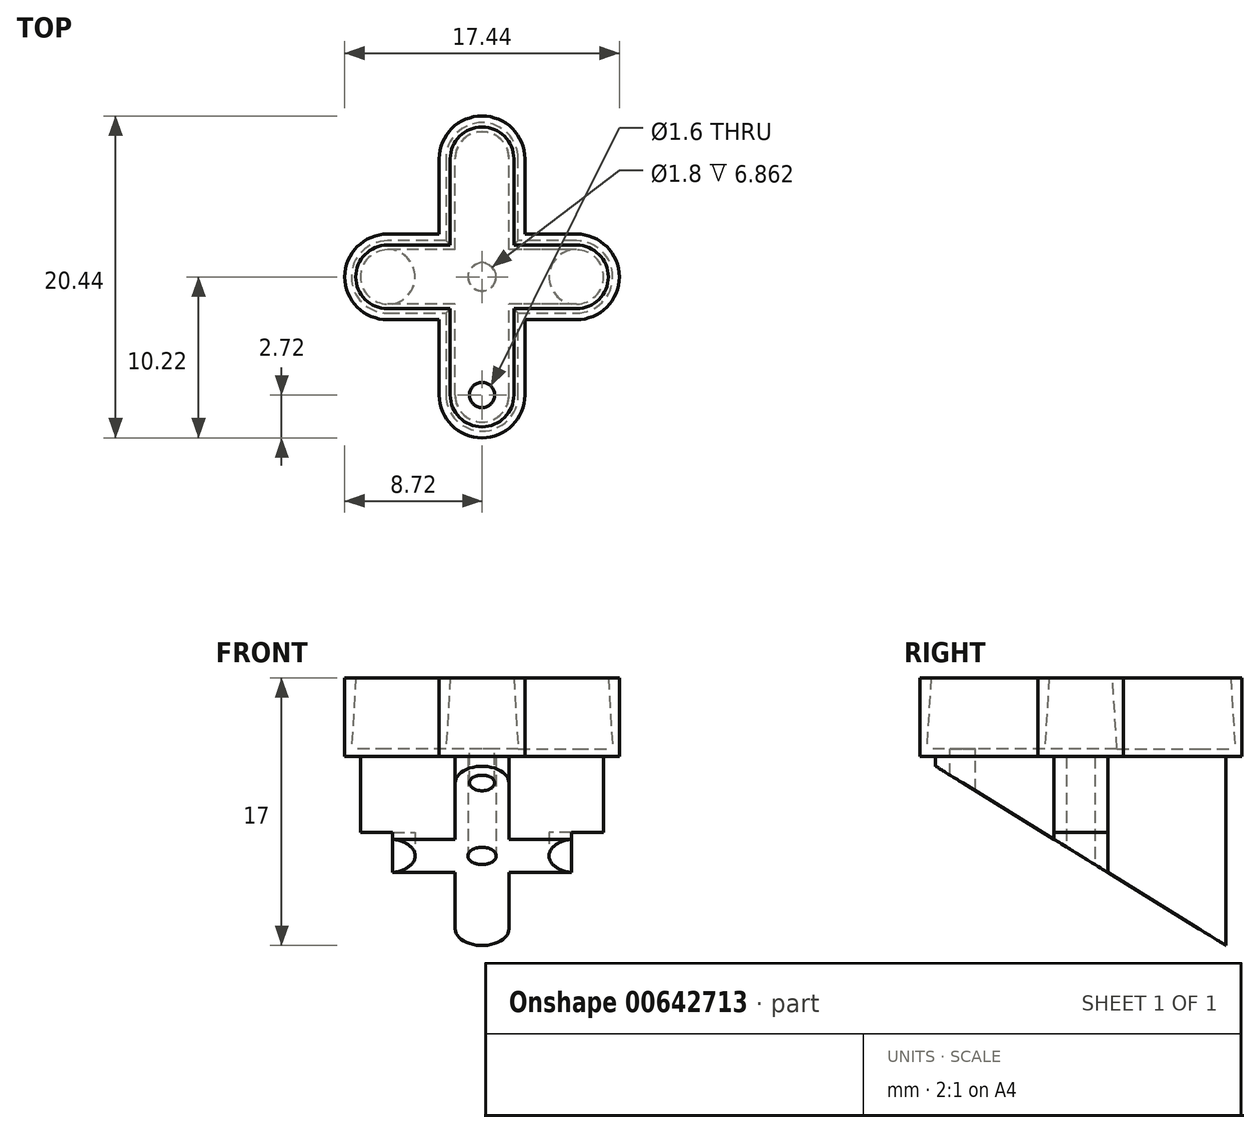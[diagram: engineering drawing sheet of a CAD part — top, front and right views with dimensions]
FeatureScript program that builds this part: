
annotation { "Feature Type Name" : "Feature", "Feature Type Description" : "" }
export const myFeature = defineFeature(function(context is Context, id is Id, definition is map)
    precondition{}
    {
        {
            var Q0;
            Q0=qCreatedBy(makeId("Top.planeOp"),FACE);
            var sketch = newSketch(context, id + "F0", { "sketchPlane" : qUnion([Q0])});
            skLineSegment(sketch, "E0.bottom", {"start": v(6, -1.72) * mm, "end": v(-6, -1.72) * mm});
            skLineSegment(sketch, "E0.top", {"start": v(6, 1.72) * mm, "end": v(-6, 1.72) * mm});
            skLineSegment(sketch, "E0.left", {"start": v(6, -1.72) * mm, "end": v(6, 1.72) * mm});
            skLineSegment(sketch, "E0.right", {"start": v(-6, -1.72) * mm, "end": v(-6, 1.72) * mm});
            skPoint(sketch, "E0.middle", {"position": v(0, 0) * mm});
            skLineSegment(sketch, "E1.bottom", {"start": v(1.72, -7.5) * mm, "end": v(-1.72, -7.5) * mm});
            skLineSegment(sketch, "E1.top", {"start": v(1.72, 7.5) * mm, "end": v(-1.72, 7.5) * mm});
            skLineSegment(sketch, "E1.left", {"start": v(1.72, -7.5) * mm, "end": v(1.72, 7.5) * mm});
            skLineSegment(sketch, "E1.right", {"start": v(-1.72, -7.5) * mm, "end": v(-1.72, 7.5) * mm});
            skArc(sketch, "E2", {"start": v(1.72, 7.5) * mm, "mid": v(0, 9.22) * mm, "end": v(-1.72, 7.5) * mm});
            skArc(sketch, "E3", {"start": v(6, -1.72) * mm, "mid": v(7.72, 0) * mm, "end": v(6, 1.72) * mm});
            skArc(sketch, "E4", {"start": v(-1.72, -7.5) * mm, "mid": v(0, -9.22) * mm, "end": v(1.72, -7.5) * mm});
            skArc(sketch, "E5", {"start": v(-6, 1.72) * mm, "mid": v(-7.72, 0) * mm, "end": v(-6, -1.72) * mm});
            skSolve(sketch);
        }
        {
            var Q0;
            Q0=qSketchRegion(id+"F0",true);
            extrude(context, id + "F1", {"entities" : qUnion([Q0]), "depth" : 12 * mm, "offsetDistance" : 25 * mm});
        }
        {
            var Q0;
            Q0=qCreatedBy(makeId("Right.planeOp"),FACE);
            var sketch = newSketch(context, id + "F2", { "sketchPlane" : qUnion([Q0])});
            skLineSegment(sketch, "E6.0.0", {"start": v(7.5, 0) * mm, "end": v(9.22, 0) * mm, "construction": true});
            skLineSegment(sketch, "E6.0.1", {"start": v(7.5, 0) * mm, "end": v(7.5, 12) * mm});
            skLineSegment(sketch, "E6.0.2", {"start": v(7.5, 12) * mm, "end": v(9.22, 12) * mm, "construction": true});
            skLineSegment(sketch, "E6.0.3", {"start": v(7.5, 12) * mm, "end": v(7.5, 0) * mm, "construction": true});
            skLineSegment(sketch, "E7.0.0", {"start": v(-7.5, 0) * mm, "end": v(-9.22, 0) * mm, "construction": true});
            skLineSegment(sketch, "E7.0.1", {"start": v(-7.5, 0) * mm, "end": v(-7.5, 12) * mm});
            skLineSegment(sketch, "E7.0.2", {"start": v(-7.5, 12) * mm, "end": v(-9.22, 12) * mm, "construction": true});
            skLineSegment(sketch, "E7.0.3", {"start": v(-7.5, 12) * mm, "end": v(-7.5, 0) * mm});
            skLineSegment(sketch, "E8", {"start": v(9.22, 0) * mm, "end": v(-9.22, 11.39) * mm});
            skLineSegment(sketch, "E9", {"start": v(-9.22, 11.39) * mm, "end": v(-9.22, 0) * mm});
            skLineSegment(sketch, "E10", {"start": v(9.22, 0) * mm, "end": v(-9.22, 0) * mm});
            skSolve(sketch);
        }
        {
            var Q0;
            Q0=qSketchRegion(id+"F2",true);
            extrude(context, id + "F3", {"entities" : qUnion([Q0]), "operationType" : NewBodyOperationType.REMOVE, "oppositeDirection" : true, "depth" : 25 * mm, "offsetDistance" : 25 * mm, "hasSecondDirection" : true, "secondDirectionOppositeDirection" : false, "secondDirectionDepth" : 25 * mm});
        }
        {
            var Q0;
            Q0=qCreatedBy(makeId("Top.planeOp"),FACE);
            var sketch = newSketch(context, id + "F4", { "sketchPlane" : qUnion([Q0])});
            skLineSegment(sketch, "E11.0", {"start": v(-1.72, 1.72) * mm, "end": v(-1.72, 7.5) * mm, "construction": true});
            skLineSegment(sketch, "E12.0", {"start": v(1.72, 1.72) * mm, "end": v(1.72, 7.5) * mm, "construction": true});
            skPoint(sketch, "E13.0", {"position": v(3.86, 1.72) * mm});
            skLineSegment(sketch, "E14.0", {"start": v(6, 1.72) * mm, "end": v(1.72, 1.72) * mm, "construction": true});
            skLineSegment(sketch, "E15.0", {"start": v(6, -1.72) * mm, "end": v(1.72, -1.72) * mm, "construction": true});
            skLineSegment(sketch, "E16.0", {"start": v(1.72, -7.5) * mm, "end": v(1.72, -1.72) * mm, "construction": true});
            skLineSegment(sketch, "E17.0", {"start": v(-1.72, -7.5) * mm, "end": v(-1.72, -1.72) * mm, "construction": true});
            skPoint(sketch, "E18.0", {"position": v(-3.86, -1.72) * mm});
            skLineSegment(sketch, "E19.0", {"start": v(-1.72, -1.72) * mm, "end": v(-6, -1.72) * mm, "construction": true});
            skPoint(sketch, "E20.0", {"position": v(-3.86, 1.72) * mm});
            skLineSegment(sketch, "E21.0", {"start": v(-1.72, 1.72) * mm, "end": v(-6, 1.72) * mm, "construction": true});
            skCircle(sketch, "E22", {"center": v(6, 0) * mm, "radius": 1.75 * mm});
            skCircle(sketch, "E23", {"center": v(-6, 0) * mm, "radius": 1.75 * mm});
            skSolve(sketch);
        }
        {
            var Q0;
            Q0=qSketchRegion(id+"F4",true);
            extrude(context, id + "F5", {"entities" : qUnion([Q0]), "operationType" : NewBodyOperationType.REMOVE, "depth" : 7.2 * mm, "offsetDistance" : 25 * mm});
        }
        {
            var Q0;
            Q0=qCreatedBy(makeId("Top.planeOp"),FACE);
            var sketch = newSketch(context, id + "F6", { "sketchPlane" : qUnion([Q0])});
            skCircle(sketch, "E24", {"center": v(0, 0) * mm, "radius": 0.9 * mm});
            skSolve(sketch);
        }
        {
            var Q0;
            Q0=qSketchRegion(id+"F6",true);
            extrude(context, id + "F7", {"entities" : qUnion([Q0]), "operationType" : NewBodyOperationType.REMOVE, "depth" : 55 * mm, "offsetDistance" : 25 * mm});
        }
        {
            var Q0;
            Q0=makeQuery(id+"F1.opExtrude","CAP_FACE",FACE,{"disambiguationData":[OSD([sQuery(id+"F0.wireOp",EDGE,"E0.bottom"),sQuery(id+"F0.wireOp",EDGE,"E0.top"),sQuery(id+"F0.wireOp",EDGE,"E1.left"),sQuery(id+"F0.wireOp",EDGE,"E1.right"),sQuery(id+"F0.wireOp",EDGE,"E2"),sQuery(id+"F0.wireOp",EDGE,"E3"),sQuery(id+"F0.wireOp",EDGE,"E4"),sQuery(id+"F0.wireOp",EDGE,"E5")])],"isStart":false});
            var sketch = newSketch(context, id + "F8", { "sketchPlane" : qUnion([Q0])});
            skLineSegment(sketch, "E25.bottom", {"start": v(15.32, -11.97) * mm, "end": v(-15.32, -11.97) * mm});
            skLineSegment(sketch, "E25.top", {"start": v(15.32, 11.97) * mm, "end": v(-15.32, 11.97) * mm});
            skLineSegment(sketch, "E25.left", {"start": v(15.32, -11.97) * mm, "end": v(15.32, 11.97) * mm});
            skLineSegment(sketch, "E25.right", {"start": v(-15.32, -11.97) * mm, "end": v(-15.32, 11.97) * mm});
            skPoint(sketch, "E25.middle", {"position": v(0, 0) * mm});
            skSolve(sketch);
        }
        {
            var Q0;
            {var subQ1=sQuery(id+"F0.wireOp",EDGE,"E2");Q0=makeQuery(id+"F8.imprint","IMPRINT",FACE,{"disambiguationData":[TD([[makeQuery(id+"F8.imprint","IMPRINT",EDGE,{"derivedFrom":makeQuery(id+"F1.opExtrude","CAP_EDGE",EDGE,{"disambiguationData":[OSD([subQ1])],"isStart":false})}),1.0]])]});}
            var sketch = newSketch(context, id + "F9", { "sketchPlane" : qUnion([Q0])});
            skLineSegment(sketch, "E26.0", {"start": v(2.72, -7.5) * mm, "end": v(2.72, -2.72) * mm});
            skArc(sketch, "E26.1", {"start": v(2.72, 7.5) * mm, "mid": v(0, 10.22) * mm, "end": v(-2.72, 7.5) * mm});
            skLineSegment(sketch, "E26.2", {"start": v(2.72, 2.72) * mm, "end": v(2.72, 7.5) * mm});
            skLineSegment(sketch, "E26.3", {"start": v(6, 2.72) * mm, "end": v(2.72, 2.72) * mm});
            skArc(sketch, "E26.4", {"start": v(6, -2.72) * mm, "mid": v(8.72, 0) * mm, "end": v(6, 2.72) * mm});
            skLineSegment(sketch, "E26.5", {"start": v(-2.72, 7.5) * mm, "end": v(-2.72, 2.72) * mm});
            skLineSegment(sketch, "E26.6", {"start": v(2.72, -2.72) * mm, "end": v(6, -2.72) * mm});
            skLineSegment(sketch, "E26.7", {"start": v(-2.72, 2.72) * mm, "end": v(-6, 2.72) * mm});
            skArc(sketch, "E26.8", {"start": v(-6, 2.72) * mm, "mid": v(-8.72, 0) * mm, "end": v(-6, -2.72) * mm});
            skLineSegment(sketch, "E26.9", {"start": v(-6, -2.72) * mm, "end": v(-2.72, -2.72) * mm});
            skLineSegment(sketch, "E26.10", {"start": v(-2.72, -2.72) * mm, "end": v(-2.72, -7.5) * mm});
            skArc(sketch, "E26.11", {"start": v(-2.72, -7.5) * mm, "mid": v(0, -10.22) * mm, "end": v(2.72, -7.5) * mm});
            skSolve(sketch);
        }
        {
            var Q0;
            {var subQ1=sQuery(id+"F0.wireOp",EDGE,"E2");Q0=makeQuery(id+"F8.imprint","IMPRINT",FACE,{"disambiguationData":[TD([[makeQuery(id+"F8.imprint","IMPRINT",EDGE,{"derivedFrom":makeQuery(id+"F1.opExtrude","CAP_EDGE",EDGE,{"disambiguationData":[OSD([subQ1])],"isStart":false})}),1.0]])]});}
            var Q1;
            Q1 = qSketchRegion(id + "F9", true);
            extrude(context, id + "F10", {"entities" : qUnion([Q0, Q1]), "operationType" : NewBodyOperationType.ADD, "depth" : 5 * mm, "offsetDistance" : 25 * mm});
        }
        {
            var Q0;
            Q0=makeQuery(id+"F10.boolean.opBoolean","MERGE",FACE,{"derivedFrom":[makeQuery(id+"F10.opExtrude","CAP_FACE",FACE,{"disambiguationData":[OSD([sQuery(id+"F0.wireOp",EDGE,"E0.bottom"),sQuery(id+"F0.wireOp",EDGE,"E0.top"),sQuery(id+"F0.wireOp",EDGE,"E1.left"),sQuery(id+"F0.wireOp",EDGE,"E1.right"),sQuery(id+"F0.wireOp",EDGE,"E2"),sQuery(id+"F0.wireOp",EDGE,"E3"),sQuery(id+"F0.wireOp",EDGE,"E4"),sQuery(id+"F0.wireOp",EDGE,"E5"),sQuery(id+"F6.wireOp",EDGE,"E24")])],"isStart":false}),makeQuery(id+"F10.opExtrude","CAP_FACE",FACE,{"disambiguationData":[OSD([sQuery(id+"F9.wireOp",EDGE,"E26.0"),sQuery(id+"F9.wireOp",EDGE,"E26.1"),sQuery(id+"F9.wireOp",EDGE,"E26.2"),sQuery(id+"F9.wireOp",EDGE,"E26.3"),sQuery(id+"F9.wireOp",EDGE,"E26.4"),sQuery(id+"F9.wireOp",EDGE,"E26.5"),sQuery(id+"F9.wireOp",EDGE,"E26.6"),sQuery(id+"F9.wireOp",EDGE,"E26.7"),sQuery(id+"F9.wireOp",EDGE,"E26.8"),sQuery(id+"F9.wireOp",EDGE,"E26.9"),sQuery(id+"F9.wireOp",EDGE,"E26.10"),sQuery(id+"F9.wireOp",EDGE,"E26.11")])],"isStart":false})]});
            var sketch = newSketch(context, id + "F11", { "sketchPlane" : qUnion([Q0])});
            skLineSegment(sketch, "E27.0", {"start": v(2.72, -7.5) * mm, "end": v(2.72, -2.72) * mm, "construction": true});
            skCircle(sketch, "E28", {"center": v(0, -7.5) * mm, "radius": 0.8 * mm});
            skSolve(sketch);
        }
        {
            var Q0;
            Q0 = qSketchRegion(id + "F11", true);
            var Q1;
            Q1=sQuery(id+"F11.wireOp",EDGE,"E28");
            extrude(context, id + "F12", {"entities" : qUnion([Q0]), "operationType" : NewBodyOperationType.REMOVE, "surfaceEntities" : qUnion([Q1]), "endBound" : BoundingType.THROUGH_ALL, "oppositeDirection" : true, "depth" : 25 * mm, "offsetDistance" : 25 * mm});
        }
        {
            var Q0;
            Q0=makeQuery(id+"F10.boolean.opBoolean","MERGE",FACE,{"derivedFrom":[makeQuery(id+"F10.opExtrude","CAP_FACE",FACE,{"disambiguationData":[OSD([sQuery(id+"F0.wireOp",EDGE,"E0.bottom"),sQuery(id+"F0.wireOp",EDGE,"E0.top"),sQuery(id+"F0.wireOp",EDGE,"E1.left"),sQuery(id+"F0.wireOp",EDGE,"E1.right"),sQuery(id+"F0.wireOp",EDGE,"E2"),sQuery(id+"F0.wireOp",EDGE,"E3"),sQuery(id+"F0.wireOp",EDGE,"E4"),sQuery(id+"F0.wireOp",EDGE,"E5"),sQuery(id+"F6.wireOp",EDGE,"E24")])],"isStart":false}),makeQuery(id+"F10.opExtrude","CAP_FACE",FACE,{"disambiguationData":[OSD([sQuery(id+"F9.wireOp",EDGE,"E26.0"),sQuery(id+"F9.wireOp",EDGE,"E26.1"),sQuery(id+"F9.wireOp",EDGE,"E26.2"),sQuery(id+"F9.wireOp",EDGE,"E26.3"),sQuery(id+"F9.wireOp",EDGE,"E26.4"),sQuery(id+"F9.wireOp",EDGE,"E26.5"),sQuery(id+"F9.wireOp",EDGE,"E26.6"),sQuery(id+"F9.wireOp",EDGE,"E26.7"),sQuery(id+"F9.wireOp",EDGE,"E26.8"),sQuery(id+"F9.wireOp",EDGE,"E26.9"),sQuery(id+"F9.wireOp",EDGE,"E26.10"),sQuery(id+"F9.wireOp",EDGE,"E26.11")])],"isStart":false})]});
            var sketch = newSketch(context, id + "F13", { "sketchPlane" : qUnion([Q0])});
            skLineSegment(sketch, "E29.0", {"start": v(-1.72, 1.72) * mm, "end": v(-1.72, 7.5) * mm});
            skArc(sketch, "E30.0", {"start": v(1.72, 7.5) * mm, "mid": v(0, 9.22) * mm, "end": v(-1.72, 7.5) * mm, "construction": true});
            skLineSegment(sketch, "E30.1", {"start": v(1.72, 1.72) * mm, "end": v(1.72, 7.5) * mm, "construction": true});
            skLineSegment(sketch, "E30.2", {"start": v(1.72, -7.5) * mm, "end": v(1.72, -1.72) * mm, "construction": true});
            skArc(sketch, "E30.3", {"start": v(-1.72, -7.5) * mm, "mid": v(0, -9.22) * mm, "end": v(1.72, -7.5) * mm, "construction": true});
            skArc(sketch, "E30.4", {"start": v(6, -1.72) * mm, "mid": v(7.72, 0) * mm, "end": v(6, 1.72) * mm, "construction": true});
            skLineSegment(sketch, "E30.5", {"start": v(6, -1.72) * mm, "end": v(1.72, -1.72) * mm, "construction": true});
            skLineSegment(sketch, "E30.6", {"start": v(-1.72, -1.72) * mm, "end": v(-6, -1.72) * mm, "construction": true});
            skArc(sketch, "E30.7", {"start": v(-6, 1.72) * mm, "mid": v(-7.72, 0) * mm, "end": v(-6, -1.72) * mm, "construction": true});
            skLineSegment(sketch, "E30.8", {"start": v(-1.72, -7.5) * mm, "end": v(-1.72, -1.72) * mm, "construction": true});
            skLineSegment(sketch, "E30.9", {"start": v(-1.72, 1.72) * mm, "end": v(-6, 1.72) * mm, "construction": true});
            skLineSegment(sketch, "E30.10", {"start": v(-1.72, 1.72) * mm, "end": v(-1.72, 7.5) * mm, "construction": true});
            skLineSegment(sketch, "E30.11", {"start": v(6, 1.72) * mm, "end": v(1.72, 1.72) * mm, "construction": true});
            skPoint(sketch, "E30.12", {"position": v(-3.86, -1.72) * mm});
            skPoint(sketch, "E30.13", {"position": v(-1.72, 4.6) * mm});
            skLineSegment(sketch, "E31.0", {"start": v(6, -2.02) * mm, "end": v(2.02, -2.02) * mm});
            skLineSegment(sketch, "E31.1", {"start": v(-2.02, 2.02) * mm, "end": v(-2.02, 7.5) * mm});
            skArc(sketch, "E31.2", {"start": v(2.02, 7.5) * mm, "mid": v(0, 9.52) * mm, "end": v(-2.02, 7.5) * mm});
            skLineSegment(sketch, "E31.3", {"start": v(2.02, 2.02) * mm, "end": v(2.02, 7.5) * mm});
            skLineSegment(sketch, "E31.4", {"start": v(6, 2.02) * mm, "end": v(2.02, 2.02) * mm});
            skLineSegment(sketch, "E31.5", {"start": v(-2.02, 2.02) * mm, "end": v(-6, 2.02) * mm});
            skArc(sketch, "E31.6", {"start": v(6, -2.02) * mm, "mid": v(8.02, 0) * mm, "end": v(6, 2.02) * mm});
            skArc(sketch, "E31.7", {"start": v(-6, 2.02) * mm, "mid": v(-8.02, 0) * mm, "end": v(-6, -2.02) * mm});
            skLineSegment(sketch, "E31.8", {"start": v(-2.02, -2.02) * mm, "end": v(-6, -2.02) * mm});
            skLineSegment(sketch, "E31.9", {"start": v(-2.02, -7.5) * mm, "end": v(-2.02, -2.02) * mm});
            skArc(sketch, "E31.10", {"start": v(-2.02, -7.5) * mm, "mid": v(0, -9.52) * mm, "end": v(2.02, -7.5) * mm});
            skLineSegment(sketch, "E31.11", {"start": v(2.02, -7.5) * mm, "end": v(2.02, -2.02) * mm});
            skSolve(sketch);
        }
        {
            var Q0;
            Q0 = qSketchRegion(id + "F13", true);
            extrude(context, id + "F14", {"entities" : qUnion([Q0]), "operationType" : NewBodyOperationType.REMOVE, "oppositeDirection" : true, "depth" : 4.5 * mm, "offsetDistance" : 25 * mm, "hasDraft" : true, "draftAngle" : 3.5 * degree});
        }
    });
